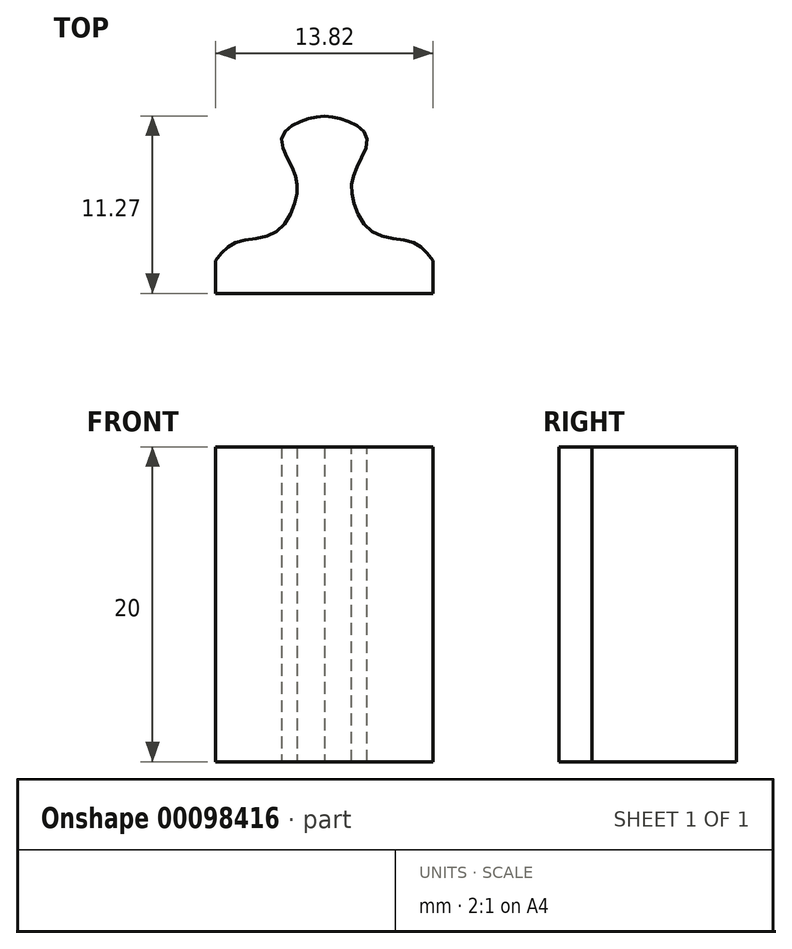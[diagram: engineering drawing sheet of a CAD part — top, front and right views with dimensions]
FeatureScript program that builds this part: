
annotation { "Feature Type Name" : "Feature", "Feature Type Description" : "" }
export const myFeature = defineFeature(function(context is Context, id is Id, definition is map)
    precondition{}
    {
        {
            var Q0;
            Q0=qCreatedBy(makeId("Top.planeOp"),FACE);
            var sketch = newSketch(context, id + "F0", { "sketchPlane" : qUnion([Q0])});
            skFitSpline(sketch, "E0", {"points": [v(0, 9.18) * mm, v(-1.44, 8.85) * mm, v(-2.7, 7.79) * mm, v(-1.99, 5.77) * mm, v(-1.8, 4.02) * mm, v(-3.13, 1.76) * mm, v(-5.59, 1.17) * mm, v(-6.9, 0) * mm], "startDerivative": vector(-11.96, -1.55) * mm, "endDerivative": vector(-9.33, -11.24) * mm});
            skLineSegment(sketch, "E1", {"start": v(-6.9, 0) * mm, "end": v(-6.9, -2.1) * mm});
            skLineSegment(sketch, "E2", {"start": v(-6.9, -2.1) * mm, "end": v(0, -2.1) * mm});
            skFitSpline(sketch, "E3.MirrorCS", {"points": [v(0, 9.18) * mm, v(1.44, 8.85) * mm, v(2.7, 7.79) * mm, v(1.99, 5.77) * mm, v(1.8, 4.02) * mm, v(3.13, 1.76) * mm, v(5.59, 1.17) * mm, v(6.9, 0) * mm], "startDerivative": vector(11.96, -1.55) * mm, "endDerivative": vector(9.33, -11.24) * mm});
            skLineSegment(sketch, "E4.MirrorCS", {"start": v(6.9, 0) * mm, "end": v(6.9, -2.1) * mm});
            skLineSegment(sketch, "E5.MirrorCS", {"start": v(6.9, -2.1) * mm, "end": v(0, -2.1) * mm});
            skLineSegment(sketch, "E6", {"start": v(0, 9.18) * mm, "end": v(0, -2.1) * mm, "construction": true});
            skSolve(sketch);
        }
        {
            var Q0;
            Q0 = qSketchRegion(id + "F0", true);
            extrude(context, id + "F1", {"entities" : qUnion([Q0]), "depth" : 20 * mm});
        }
    });
